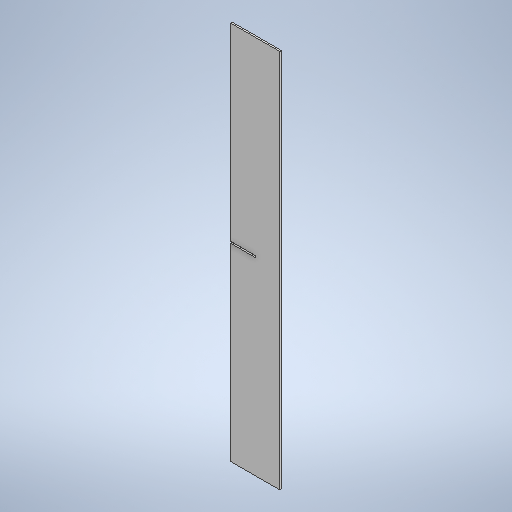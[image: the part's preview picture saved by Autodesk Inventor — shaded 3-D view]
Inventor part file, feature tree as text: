
AUTODESK INVENTOR PART (.ipt)
format: ipt  version: 2025 (Build 290162010, 162A)  size: 303,104 bytes
history: native  units: mm
features: other x3, sketch x2, sheet_metal_op x1, extrude x1, projected_geometry x1
ambient origin geometry x8: Origin, YZ Plane, XZ Plane, XY Plane, X Axis, Y Axis, Z Axis, Center Point
bodies: Body1 (feature_tree)
feature tree (8):
  other  "BSH 045 stringer 1"
  sheet_metal_op  "Face2"
  extrude  "Extrusion2"  Depth=700.0mm
  sketch  "Sketch6"  dims[d26=90.834574mm d27=700.0mm]
  other  "Plate4"
  sketch  "Sketch7"  dims[d28=3.0mm d29=46.417287mm d30=3.2mm d31=348.4mm d32=0.0mm d33=0.0mm]
  projected_geometry  "Projected Loop1"
  other  "Definition1"
